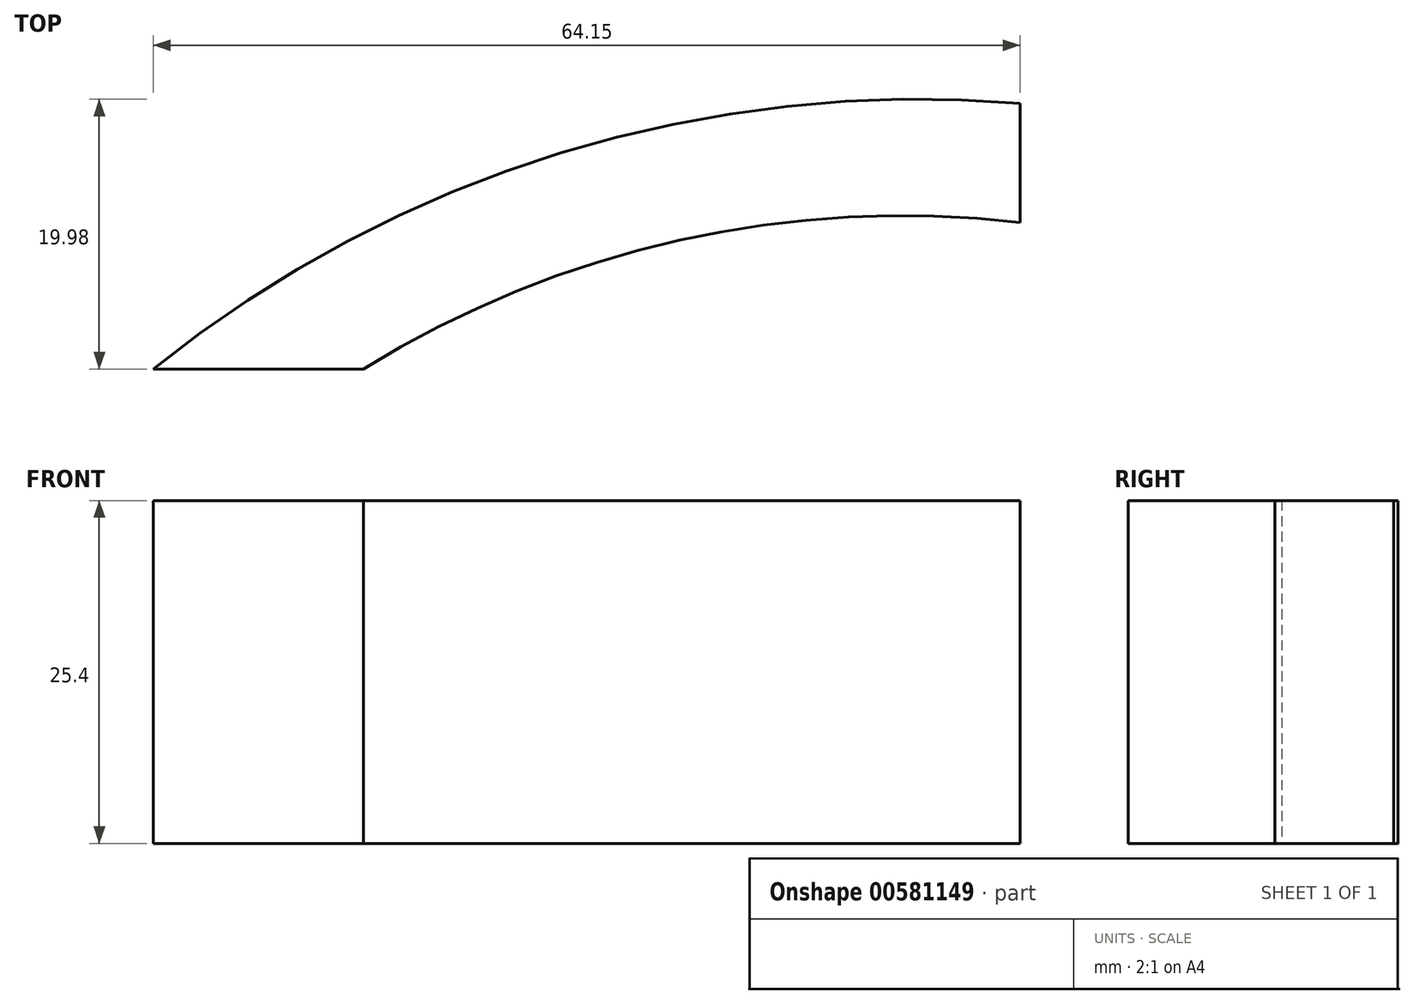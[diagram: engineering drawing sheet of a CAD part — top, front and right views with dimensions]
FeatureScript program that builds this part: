
annotation { "Feature Type Name" : "Feature", "Feature Type Description" : "" }
export const myFeature = defineFeature(function(context is Context, id is Id, definition is map)
    precondition{}
    {
        {
            var Q0;
            Q0=qCreatedBy(makeId("Top.planeOp"),FACE);
            var sketch = newSketch(context, id + "F0", { "sketchPlane" : qUnion([Q0])});
            skArc(sketch, "E0", {"start": v(0, 0) * mm, "mid": v(-33.97, -3.65) * mm, "end": v(-64.15, -19.67) * mm});
            skLineSegment(sketch, "E1", {"start": v(-64.15, -19.67) * mm, "end": v(-48.6, -19.67) * mm});
            skArc(sketch, "E2", {"start": v(0, -8.8) * mm, "mid": v(-25.21, -10.14) * mm, "end": v(-48.6, -19.67) * mm});
            skLineSegment(sketch, "E3", {"start": v(0, 0) * mm, "end": v(0, -8.8) * mm});
            skSolve(sketch);
        }
        {
            var Q0;
            Q0 = qSketchRegion(id + "F0", true);
            extrude(context, id + "F1", {"entities" : qUnion([Q0]), "depth" : 25.4 * mm, "offsetDistance" : 25.4 * mm});
        }
    });
